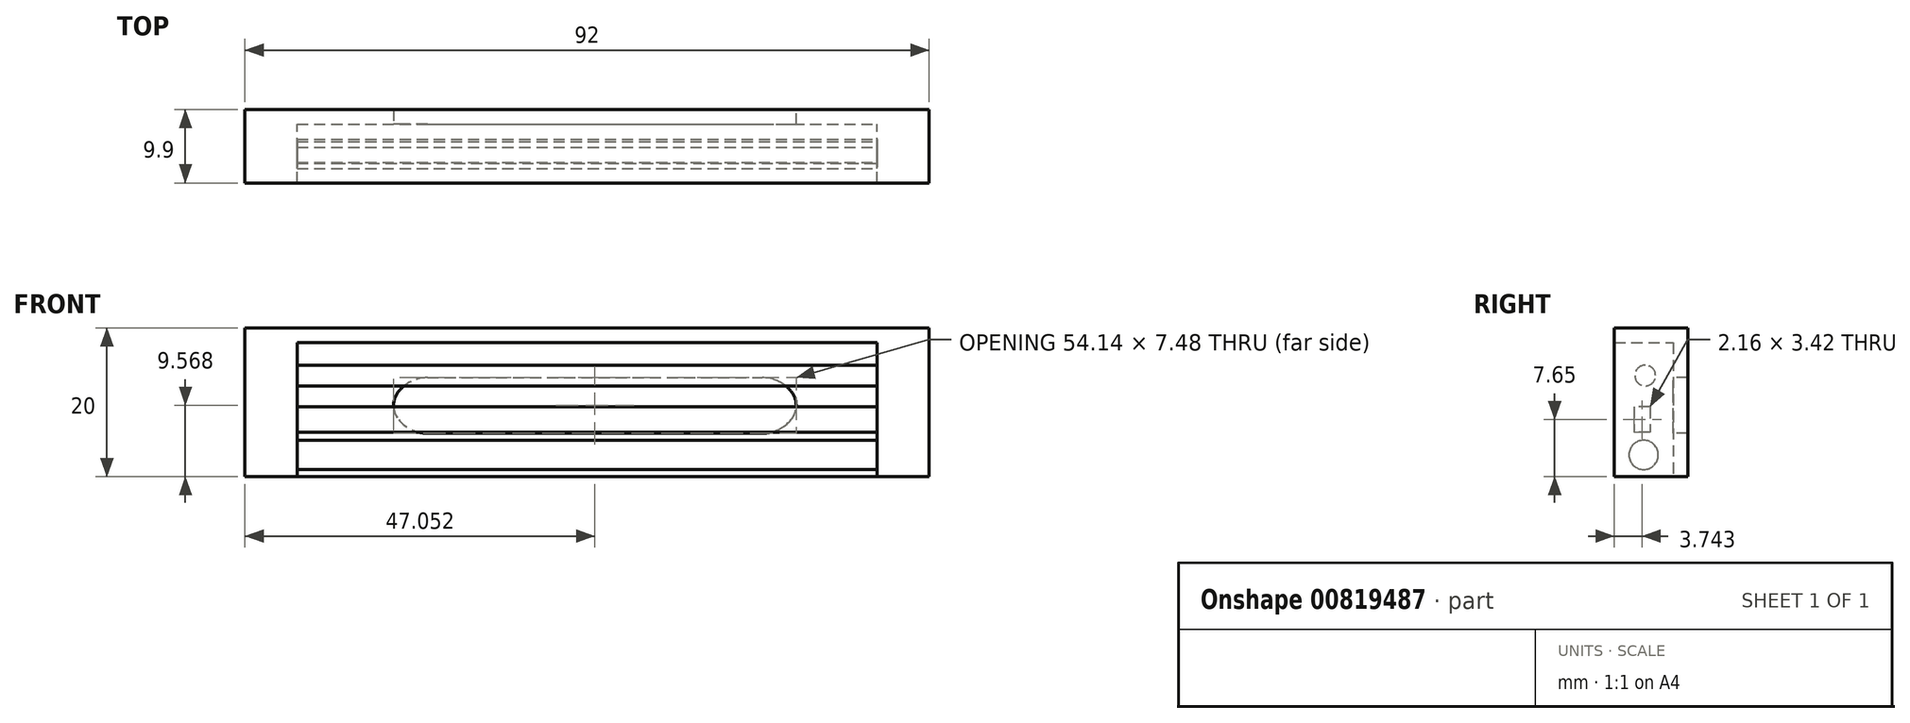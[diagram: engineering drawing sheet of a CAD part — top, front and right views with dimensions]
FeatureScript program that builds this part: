
annotation { "Feature Type Name" : "Feature", "Feature Type Description" : "" }
export const myFeature = defineFeature(function(context is Context, id is Id, definition is map)
    precondition{}
    {
        {
            var Q0;
            Q0=qCreatedBy(makeId("Top.planeOp"),FACE);
            var sketch = newSketch(context, id + "F0", { "sketchPlane" : qUnion([Q0])});
            skLineSegment(sketch, "E0.bottom", {"start": v(-75.33, -54.86) * mm, "end": v(6.67, -54.86) * mm});
            skLineSegment(sketch, "E0.top", {"start": v(-75.33, -44.96) * mm, "end": v(6.67, -44.96) * mm});
            skLineSegment(sketch, "E0.left", {"start": v(-75.33, -54.86) * mm, "end": v(-75.33, -44.96) * mm});
            skLineSegment(sketch, "E0.right", {"start": v(6.67, -54.86) * mm, "end": v(6.67, -44.96) * mm});
            skSolve(sketch);
        }
        {
            var Q0;
            Q0=makeQuery(id+"F0.imprint","IMPRINT",FACE,{"disambiguationData":[TD([[makeQuery(id+"F0.imprint","IMPRINT",EDGE,{"derivedFrom":sQuery(id+"F0.wireOp",EDGE,"E0.bottom")}),1.0]])]});
            extrude(context, id + "F1", {"entities" : qUnion([Q0]), "depth" : 20 * mm, "offsetDistance" : 25 * mm});
        }
        {
            var Q0;
            Q0=makeQuery(id+"F1.opExtrude","SWEPT_FACE",FACE,{"disambiguationData":[OSD([sQuery(id+"F0.wireOp",EDGE,"E0.bottom")])]});
            shell(context, id + "F2", {"entities" : qUnion([Q0]), "thickness" : 2 * mm});
        }
        {
            var Q0;
            {var subQ0=sQuery(id+"F0.wireOp",EDGE,"E0.right");var subQ1=sQuery(id+"F0.wireOp",EDGE,"E0.left");var subQ2=sQuery(id+"F0.wireOp",EDGE,"E0.top");var subQ3=sQuery(id+"F0.wireOp",EDGE,"E0.bottom");Q0=makeQuery(id+"F2.opShell","OFFSET_FACE",FACE,{"disambiguationData":[OSD([subQ3,subQ2,subQ1,subQ0]),TDD([makeQuery(id+"F1.opExtrude","CAP_FACE",FACE,{"disambiguationData":[OSD([subQ3,subQ2,subQ1,subQ0])],"isStart":true})])]});}
            extrude(context, id + "F3", {"entities" : qUnion([Q0]), "operationType" : NewBodyOperationType.REMOVE, "oppositeDirection" : true, "depth" : 2 * mm, "offsetDistance" : 25 * mm});
        }
        {
            var Q0;
            {var subQ0=sQuery(id+"F0.wireOp",EDGE,"E0.right");Q0=makeQuery(id+"F3.boolean.opBoolean","MERGE",FACE,{"derivedFrom":[makeQuery(id+"F2.opShell","OFFSET_FACE",FACE,{"disambiguationData":[OSD([subQ0])]}),makeQuery(id+"F3.opExtrude","SWEPT_FACE",FACE,{"disambiguationData":[OSD([subQ0])]})]});}
            extrude(context, id + "F4", {"entities" : qUnion([Q0]), "operationType" : NewBodyOperationType.ADD, "depth" : 5 * mm, "offsetDistance" : 25 * mm});
        }
        {
            var Q0;
            Q0=makeQuery(id+"F4.opExtrude","CAP_FACE",FACE,{"disambiguationData":[OSD([sQuery(id+"F0.wireOp",EDGE,"E0.right")])],"isStart":false});
            var sketch = newSketch(context, id + "F5", { "sketchPlane" : qUnion([Q0])});
            skCircle(sketch, "E1", {"center": v(50.9, 2.92) * mm, "radius": 1.97 * mm});
            skPoint(sketch, "E1.centerSnap0", {"position": v(50.9, 0) * mm});
            skSolve(sketch);
        }
        {
            var Q0;
            Q0=makeQuery(id+"F5.imprint","IMPRINT",FACE,{"disambiguationData":[TD([[makeQuery(id+"F5.imprint","IMPRINT",EDGE,{"derivedFrom":sQuery(id+"F5.wireOp",EDGE,"E1")}),-1.0]])]});
            var sketch = newSketch(context, id + "F6", { "sketchPlane" : qUnion([Q0])});
            skCircle(sketch, "E2", {"center": v(50.7, 13.6) * mm, "radius": 1.4 * mm});
            skSolve(sketch);
        }
        {
            var Q0;
            Q0=makeQuery(id+"F6.imprint","IMPRINT",FACE,{"disambiguationData":[TD([[makeQuery(id+"F6.imprint","IMPRINT",EDGE,{"derivedFrom":sQuery(id+"F6.wireOp",EDGE,"E2")}),1.0]])]});
            var Q1;
            Q1=makeQuery(id+"F5.imprint","IMPRINT",FACE,{"disambiguationData":[TD([[makeQuery(id+"F5.imprint","IMPRINT",EDGE,{"derivedFrom":sQuery(id+"F5.wireOp",EDGE,"E1")}),1.0]])]});
            extrude(context, id + "F7", {"entities" : qUnion([Q0, Q1]), "operationType" : NewBodyOperationType.ADD, "depth" : 74 * mm, "offsetDistance" : 25 * mm});
        }
        {
            var Q0;
            {var subQ0=sQuery(id+"F0.wireOp",EDGE,"E0.top");Q0=makeQuery(id+"F3.boolean.opBoolean","MERGE",FACE,{"derivedFrom":[makeQuery(id+"F2.opShell","OFFSET_FACE",FACE,{"disambiguationData":[OSD([subQ0])]}),makeQuery(id+"F3.opExtrude","SWEPT_FACE",FACE,{"disambiguationData":[OSD([subQ0])]})]});}
            var sketch = newSketch(context, id + "F8", { "sketchPlane" : qUnion([Q0])});
            skLineSegment(sketch, "E3.bottom", {"start": v(-65.8, 13.3) * mm, "end": v(-10.76, 13.3) * mm});
            skLineSegment(sketch, "E3.top", {"start": v(-65.8, 5.83) * mm, "end": v(-10.76, 5.83) * mm});
            skLineSegment(sketch, "E3.left", {"start": v(-65.8, 13.3) * mm, "end": v(-65.8, 5.83) * mm});
            skLineSegment(sketch, "E3.right", {"start": v(-10.76, 13.3) * mm, "end": v(-10.76, 5.83) * mm});
            skSolve(sketch);
        }
        {
            var Q0;
            Q0=makeQuery(id+"F8.imprint","IMPRINT",FACE,{"disambiguationData":[TD([[makeQuery(id+"F8.imprint","IMPRINT",EDGE,{"derivedFrom":sQuery(id+"F8.wireOp",EDGE,"E3.bottom")}),-1.0]])]});
            extrude(context, id + "F9", {"entities" : qUnion([Q0]), "operationType" : NewBodyOperationType.REMOVE, "oppositeDirection" : true, "depth" : 2 * mm, "offsetDistance" : 25 * mm});
        }
        {
            var Q0;
            Q0=makeQuery(id+"F9.boolean.opBoolean","COPY",EDGE,{"derivedFrom":makeQuery(id+"F9.opExtrude","SWEPT_EDGE",EDGE,{"disambiguationData":[OSD([sQuery(id+"F8.wireOp",EDGE,"E3.top"),sQuery(id+"F8.wireOp",EDGE,"E3.right")])]})});
            var Q1;
            Q1=makeQuery(id+"F9.boolean.opBoolean","COPY",EDGE,{"derivedFrom":makeQuery(id+"F9.opExtrude","SWEPT_EDGE",EDGE,{"disambiguationData":[OSD([sQuery(id+"F8.wireOp",EDGE,"E3.top"),sQuery(id+"F8.wireOp",EDGE,"E3.left")])]})});
            var Q2;
            Q2=makeQuery(id+"F9.boolean.opBoolean","COPY",EDGE,{"derivedFrom":makeQuery(id+"F9.opExtrude","SWEPT_EDGE",EDGE,{"disambiguationData":[OSD([sQuery(id+"F8.wireOp",EDGE,"E3.bottom"),sQuery(id+"F8.wireOp",EDGE,"E3.left")])]})});
            var Q3;
            Q3=makeQuery(id+"F9.boolean.opBoolean","COPY",EDGE,{"derivedFrom":makeQuery(id+"F9.opExtrude","SWEPT_EDGE",EDGE,{"disambiguationData":[OSD([sQuery(id+"F8.wireOp",EDGE,"E3.bottom"),sQuery(id+"F8.wireOp",EDGE,"E3.right")])]})});
            fillet(context, id + "F10", {"entities" : qUnion([Q0, Q1, Q2, Q3]), "radius" : 5 * mm, "tangentPropagation" : true, "allowEdgeOverflow" : false});
        }
        {
            var Q0;
            {var subQ0=sQuery(id+"F8.wireOp",EDGE,"E3.right");Q0=makeQuery(id+"F10.opFillet","BLEND_EDGE",EDGE,{"blendedFrom":[makeQuery(id+"F9.boolean.opBoolean","COPY",EDGE,{"derivedFrom":makeQuery(id+"F9.opExtrude","SWEPT_EDGE",EDGE,{"disambiguationData":[OSD([sQuery(id+"F8.wireOp",EDGE,"E3.bottom"),subQ0])]})}),makeQuery(id+"F9.boolean.opBoolean","COPY",EDGE,{"derivedFrom":makeQuery(id+"F9.opExtrude","SWEPT_EDGE",EDGE,{"disambiguationData":[OSD([sQuery(id+"F8.wireOp",EDGE,"E3.top"),subQ0])]})})],"blendedInto":[]});}
            var Q1;
            {var subQ0=sQuery(id+"F8.wireOp",EDGE,"E3.left");Q1=makeQuery(id+"F10.opFillet","BLEND_EDGE",EDGE,{"blendedFrom":[makeQuery(id+"F9.boolean.opBoolean","COPY",EDGE,{"derivedFrom":makeQuery(id+"F9.opExtrude","SWEPT_EDGE",EDGE,{"disambiguationData":[OSD([sQuery(id+"F8.wireOp",EDGE,"E3.bottom"),subQ0])]})}),makeQuery(id+"F9.boolean.opBoolean","COPY",EDGE,{"derivedFrom":makeQuery(id+"F9.opExtrude","SWEPT_EDGE",EDGE,{"disambiguationData":[OSD([sQuery(id+"F8.wireOp",EDGE,"E3.top"),subQ0])]})})],"blendedInto":[]});}
            fillet(context, id + "F11", {"entities" : qUnion([Q0, Q1]), "radius" : 3 * mm, "allowEdgeOverflow" : false});
        }
        {
            var Q0;
            Q0=makeQuery(id+"F4.opExtrude","CAP_FACE",FACE,{"disambiguationData":[OSD([sQuery(id+"F0.wireOp",EDGE,"E0.right")])],"isStart":false});
            var sketch = newSketch(context, id + "F12", { "sketchPlane" : qUnion([Q0])});
            skLineSegment(sketch, "E4.bottom", {"start": v(50.2, 9.36) * mm, "end": v(52.02, 9.36) * mm});
            skLineSegment(sketch, "E4.top", {"start": v(50.2, 5.94) * mm, "end": v(52.02, 5.94) * mm});
            skLineSegment(sketch, "E4.left", {"start": v(50.2, 9.36) * mm, "end": v(50.2, 5.94) * mm});
            skLineSegment(sketch, "E4.right", {"start": v(52.02, 9.36) * mm, "end": v(52.02, 5.94) * mm});
            skSolve(sketch);
        }
        {
            var Q0;
            Q0=makeQuery(id+"F12.imprint","IMPRINT",FACE,{"disambiguationData":[TD([[makeQuery(id+"F12.imprint","IMPRINT",EDGE,{"derivedFrom":sQuery(id+"F12.wireOp",EDGE,"E4.bottom")}),-1.0]])]});
            extrude(context, id + "F13", {"entities" : qUnion([Q0]), "operationType" : NewBodyOperationType.ADD, "depth" : 1 * mm, "offsetDistance" : 25 * mm});
        }
        {
            var Q0;
            Q0=makeQuery(id+"F13.opExtrude","CAP_EDGE",EDGE,{"disambiguationData":[OSD([sQuery(id+"F12.wireOp",EDGE,"E4.right")])],"isStart":false});
            var Q1;
            Q1=makeQuery(id+"F13.opExtrude","CAP_EDGE",EDGE,{"disambiguationData":[OSD([sQuery(id+"F12.wireOp",EDGE,"E4.left")])],"isStart":false});
            fillet(context, id + "F14", {"entities" : qUnion([Q0, Q1]), "radius" : 2 * mm, "tangentPropagation" : true, "allowEdgeOverflow" : false});
        }
        {
            var Q0;
            Q0=makeQuery(id+"F14.opFillet","BLEND_EDGE",EDGE,{"blendedFrom":[makeQuery(id+"F13.opExtrude","CAP_EDGE",EDGE,{"disambiguationData":[OSD([sQuery(id+"F12.wireOp",EDGE,"E4.left")])],"isStart":false}),makeQuery(id+"F13.opExtrude","CAP_EDGE",EDGE,{"disambiguationData":[OSD([sQuery(id+"F12.wireOp",EDGE,"E4.right")])],"isStart":false})],"blendedInto":[]});
            fillet(context, id + "F15", {"entities" : qUnion([Q0]), "radius" : .7 * mm, "tangentPropagation" : true, "allowEdgeOverflow" : false});
        }
        {
            var Q0;
            Q0=makeQuery(id+"F4.opExtrude","CAP_FACE",FACE,{"disambiguationData":[OSD([sQuery(id+"F0.wireOp",EDGE,"E0.right")])],"isStart":false});
            var sketch = newSketch(context, id + "F16", { "sketchPlane" : qUnion([Q0])});
            skLineSegment(sketch, "E5.bottom", {"start": v(50.04, 9.36) * mm, "end": v(52.2, 9.36) * mm});
            skLineSegment(sketch, "E5.top", {"start": v(50.04, 5.94) * mm, "end": v(52.2, 5.94) * mm});
            skLineSegment(sketch, "E5.left", {"start": v(50.04, 9.36) * mm, "end": v(50.04, 5.94) * mm});
            skLineSegment(sketch, "E5.right", {"start": v(52.2, 9.36) * mm, "end": v(52.2, 5.94) * mm});
            skSolve(sketch);
        }
        {
            var Q0;
            {var subQ2=sQuery(id+"F16.wireOp",EDGE,"E5.left");Q0=makeQuery(id+"F16.imprint","IMPRINT",FACE,{"disambiguationData":[TD([[makeQuery(id+"F16.imprint","IMPRINT",EDGE,{"derivedFrom":subQ2}),1.0]])]});}
            var Q1;
            {var subQ2=sQuery(id+"F16.wireOp",EDGE,"E5.right");Q1=makeQuery(id+"F16.imprint","IMPRINT",FACE,{"disambiguationData":[TD([[makeQuery(id+"F16.imprint","IMPRINT",EDGE,{"derivedFrom":subQ2}),-1.0]])]});}
            extrude(context, id + "F17", {"entities" : qUnion([Q0, Q1]), "operationType" : NewBodyOperationType.ADD, "depth" : 73 * mm, "offsetDistance" : 25 * mm});
        }
        {
            var Q0;
            Q0=makeQuery(id+"F17.opExtrude","SWEPT_FACE",FACE,{"disambiguationData":[OSD([sQuery(id+"F0.wireOp",EDGE,"E0.right"),sQuery(id+"F12.wireOp",EDGE,"E4.left")])]});
            extrude(context, id + "F18", {"entities" : qUnion([Q0]), "operationType" : NewBodyOperationType.ADD, "depth" : 2 * mm, "offsetDistance" : 25 * mm});
        }
        {
            var Q0;
            Q0=makeQuery(id+"F1.opExtrude","SWEPT_FACE",FACE,{"disambiguationData":[OSD([sQuery(id+"F0.wireOp",EDGE,"E0.left")])]});
            extrude(context, id + "F19", {"entities" : qUnion([Q0]), "operationType" : NewBodyOperationType.ADD, "depth" : 10 * mm, "offsetDistance" : 25 * mm});
        }
        {
            var Q0;
            {var subQ0=sQuery(id+"F0.wireOp",EDGE,"E0.left");Q0=makeQuery(id+"F3.boolean.opBoolean","MERGE",FACE,{"derivedFrom":[makeQuery(id+"F2.opShell","OFFSET_FACE",FACE,{"disambiguationData":[OSD([subQ0])]}),makeQuery(id+"F3.opExtrude","SWEPT_FACE",FACE,{"disambiguationData":[OSD([subQ0])]})]});}
            extrude(context, id + "F20", {"entities" : qUnion([Q0]), "operationType" : NewBodyOperationType.REMOVE, "oppositeDirection" : true, "depth" : 5 * mm, "offsetDistance" : 25 * mm});
        }
    });
